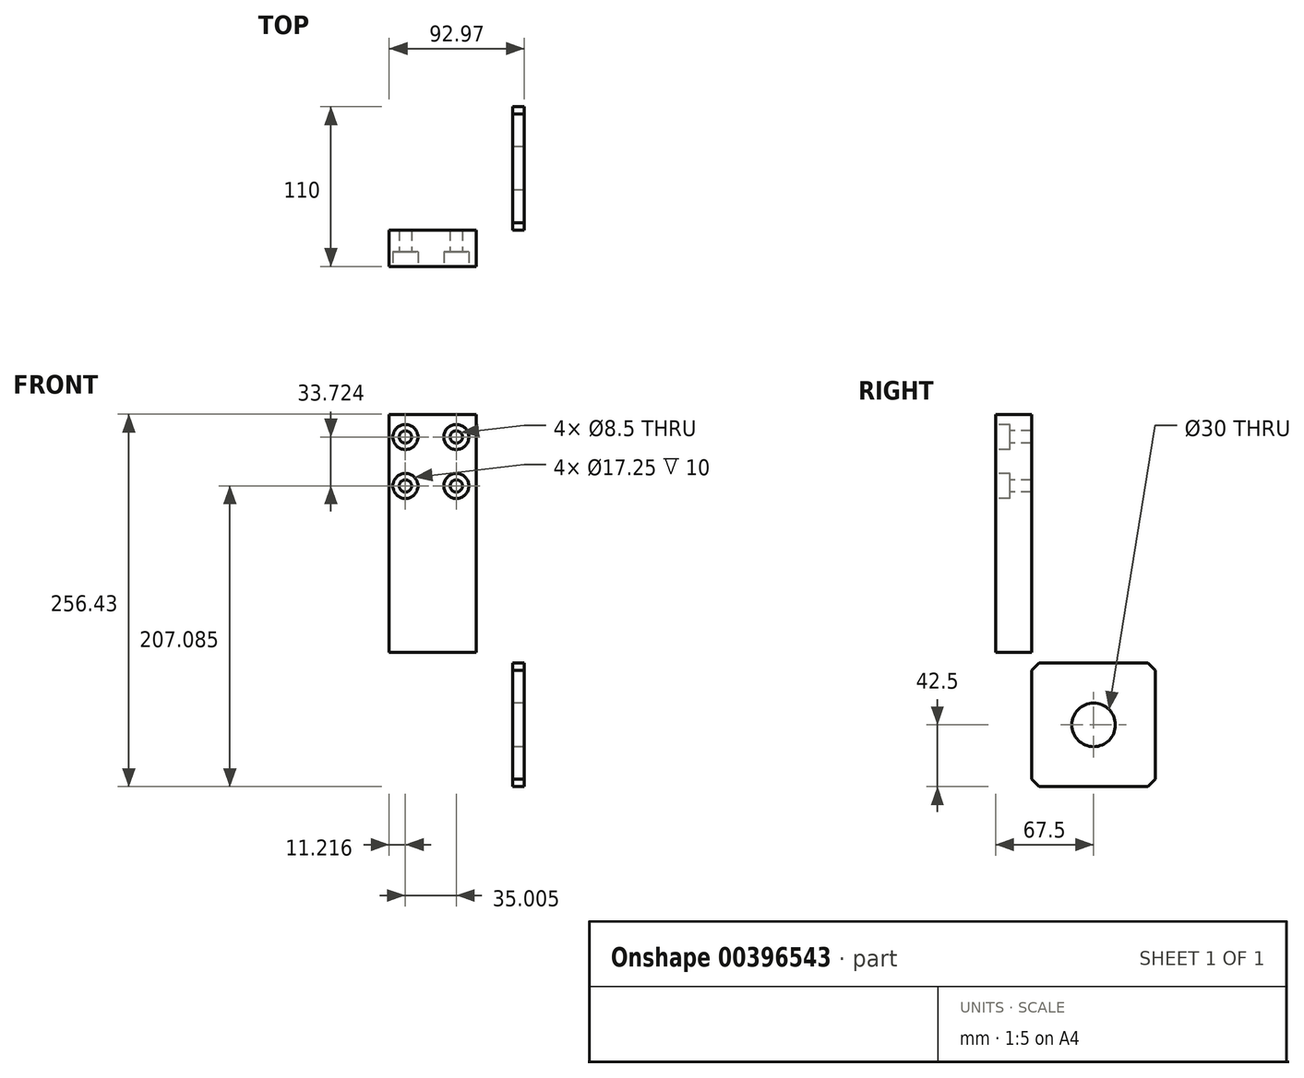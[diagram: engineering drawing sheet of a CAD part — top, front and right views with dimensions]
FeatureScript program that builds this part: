
annotation { "Feature Type Name" : "Feature", "Feature Type Description" : "" }
export const myFeature = defineFeature(function(context is Context, id is Id, definition is map)
    precondition{}
    {
        {
            var Q0;
            Q0=qCreatedBy(makeId("Right.planeOp"),FACE);
            var sketch = newSketch(context, id + "F0", { "sketchPlane" : qUnion([Q0])});
            skLineSegment(sketch, "E0.bottom", {"start": v(0, 0) * mm, "end": v(85, 0) * mm});
            skLineSegment(sketch, "E0.top", {"start": v(0, -85) * mm, "end": v(85, -85) * mm});
            skLineSegment(sketch, "E0.left", {"start": v(0, 0) * mm, "end": v(0, -85) * mm});
            skLineSegment(sketch, "E0.right", {"start": v(85, 0) * mm, "end": v(85, -85) * mm});
            skLineSegment(sketch, "E1", {"start": v(0, 0) * mm, "end": v(85, -85) * mm, "construction": true});
            skLineSegment(sketch, "E2", {"start": v(0, -85) * mm, "end": v(85, 0) * mm, "construction": true});
            skCircle(sketch, "E3", {"center": v(42.5, -42.5) * mm, "radius": 15 * mm});
            skLineSegment(sketch, "E4", {"start": v(-5.52, -8) * mm, "end": v(99.14, -8) * mm, "construction": true});
            skLineSegment(sketch, "E5", {"start": v(-7.18, -81) * mm, "end": v(94.82, -81) * mm, "construction": true});
            skLineSegment(sketch, "E6", {"start": v(7.86, 5.68) * mm, "end": v(7.86, -95.2) * mm, "construction": true});
            skLineSegment(sketch, "E7", {"start": v(0, -49.14) * mm, "end": v(7.86, -49.14) * mm, "construction": true});
            skLineSegment(sketch, "E8", {"start": v(77.14, 8.22) * mm, "end": v(77.14, -107.63) * mm, "construction": true});
            skSolve(sketch);
        }
        {
            var Q0;
            Q0=makeQuery(id+"F0.imprint","IMPRINT",FACE,{"disambiguationData":[TD([[makeQuery(id+"F0.imprint","IMPRINT",EDGE,{"derivedFrom":sQuery(id+"F0.wireOp",EDGE,"E0.bottom")}),-1.0]])]});
            extrude(context, id + "F1", {"entities" : qUnion([Q0]), "depth" : 8 * mm});
        }
        {
            var Q0;
            Q0=makeQuery(id+"F1.opExtrude","SWEPT_EDGE",EDGE,{"disambiguationData":[OSD([sQuery(id+"F0.wireOp",EDGE,"E0.bottom"),sQuery(id+"F0.wireOp",EDGE,"E0.right")])]});
            chamfer(context, id + "F2", {"entities" : qUnion([Q0]), "width" : 5 * mm, "tangentPropagation" : true});
        }
        {
            var Q0;
            Q0=makeQuery(id+"F1.opExtrude","SWEPT_EDGE",EDGE,{"disambiguationData":[OSD([sQuery(id+"F0.wireOp",EDGE,"E0.bottom"),sQuery(id+"F0.wireOp",EDGE,"E0.left")])]});
            var Q1;
            Q1=makeQuery(id+"F1.opExtrude","SWEPT_EDGE",EDGE,{"disambiguationData":[OSD([sQuery(id+"F0.wireOp",EDGE,"E0.top"),sQuery(id+"F0.wireOp",EDGE,"E0.left")])]});
            var Q2;
            Q2=makeQuery(id+"F1.opExtrude","SWEPT_EDGE",EDGE,{"disambiguationData":[OSD([sQuery(id+"F0.wireOp",EDGE,"E0.top"),sQuery(id+"F0.wireOp",EDGE,"E0.right")])]});
            chamfer(context, id + "F3", {"entities" : qUnion([Q0, Q1, Q2]), "width" : 5 * mm, "tangentPropagation" : true});
        }
        {
            var Q0;
            Q0=qCreatedBy(makeId("Front.planeOp"),FACE);
            var sketch = newSketch(context, id + "F4", { "sketchPlane" : qUnion([Q0])});
            skLineSegment(sketch, "E9.bottom", {"start": v(-84.97, 171.43) * mm, "end": v(-24.97, 171.43) * mm});
            skLineSegment(sketch, "E9.top", {"start": v(-84.97, 7.43) * mm, "end": v(-24.97, 7.43) * mm});
            skLineSegment(sketch, "E9.left", {"start": v(-84.97, 171.43) * mm, "end": v(-84.97, 7.43) * mm});
            skLineSegment(sketch, "E9.right", {"start": v(-24.97, 171.43) * mm, "end": v(-24.97, 7.43) * mm});
            skPoint(sketch, "E10", {"position": v(-72.59, 151.16) * mm});
            skPoint(sketch, "E11", {"position": v(-46.96, 151.16) * mm});
            skSolve(sketch);
        }
        {
            var Q0;
            Q0=qSketchRegion(id+"F4",true);
            extrude(context, id + "F5", {"entities" : qUnion([Q0]), "depth" : 25 * mm});
        }
        {
            var Q0;
            Q0=makeQuery(id+"F5.opExtrude","CAP_FACE",FACE,{"disambiguationData":[OSD([sQuery(id+"F4.wireOp",EDGE,"E9.bottom"),sQuery(id+"F4.wireOp",EDGE,"E9.top"),sQuery(id+"F4.wireOp",EDGE,"E9.left"),sQuery(id+"F4.wireOp",EDGE,"E9.right")])],"isStart":false});
            var sketch = newSketch(context, id + "F6", { "sketchPlane" : qUnion([Q0])});
            skPoint(sketch, "E12", {"position": v(-73.75, 155.8) * mm});
            skPoint(sketch, "E13", {"position": v(-38.75, 155.8) * mm});
            skPoint(sketch, "E14", {"position": v(-73.75, 122.09) * mm});
            skPoint(sketch, "E15", {"position": v(-38.75, 122.09) * mm});
            skSolve(sketch);
        }
        {
            var Q0;
            Q0=sQuery(id+"F6.wireOp",VERTEX,"E12");
            var Q1;
            Q1=sQuery(id+"F6.wireOp",VERTEX,"E13");
            var Q2;
            Q2=sQuery(id+"F6.wireOp",VERTEX,"E15");
            var Q3;
            Q3=sQuery(id+"F6.wireOp",VERTEX,"E14");
            var Q4;
            Q4=makeQuery(id+"F5.opExtrude","SWEPT_BODY",BODY,{"disambiguationData":[OSD([sQuery(id+"F4.wireOp",EDGE,"E9.bottom"),sQuery(id+"F4.wireOp",EDGE,"E9.top"),sQuery(id+"F4.wireOp",EDGE,"E9.left"),sQuery(id+"F4.wireOp",EDGE,"E9.right")])]});
            hole(context, id + "F7", {"style" : HoleStyle.C_BORE, "endStyle" : HoleEndStyle.THROUGH, "standardTappedOrClearance" : lookupTablePath({ "standard" : "ISO", "engagement" : "75%", "pitch" : "1.5 mm", "size" : "M10", "type" : "Tapped" }), "standardBlindInLast" : lookupTablePath({ "standard" : "ISO", "engagement" : "75%", "pitch" : "1.5 mm", "size" : "M10", "type" : "Tapped" }), "holeDiameter" : 8.5 * mm, "cBoreDiameter" : 17.25 * mm, "cBoreDepth" : 10 * mm, "startFromSketch" : true, "locations" : qUnion([Q0, Q1, Q2, Q3]), "scope" : qUnion([Q4]), "isTappedThrough" : true, "majorDiameter" : 10 * mm, "showTappedDepth" : true});
        }
    });
